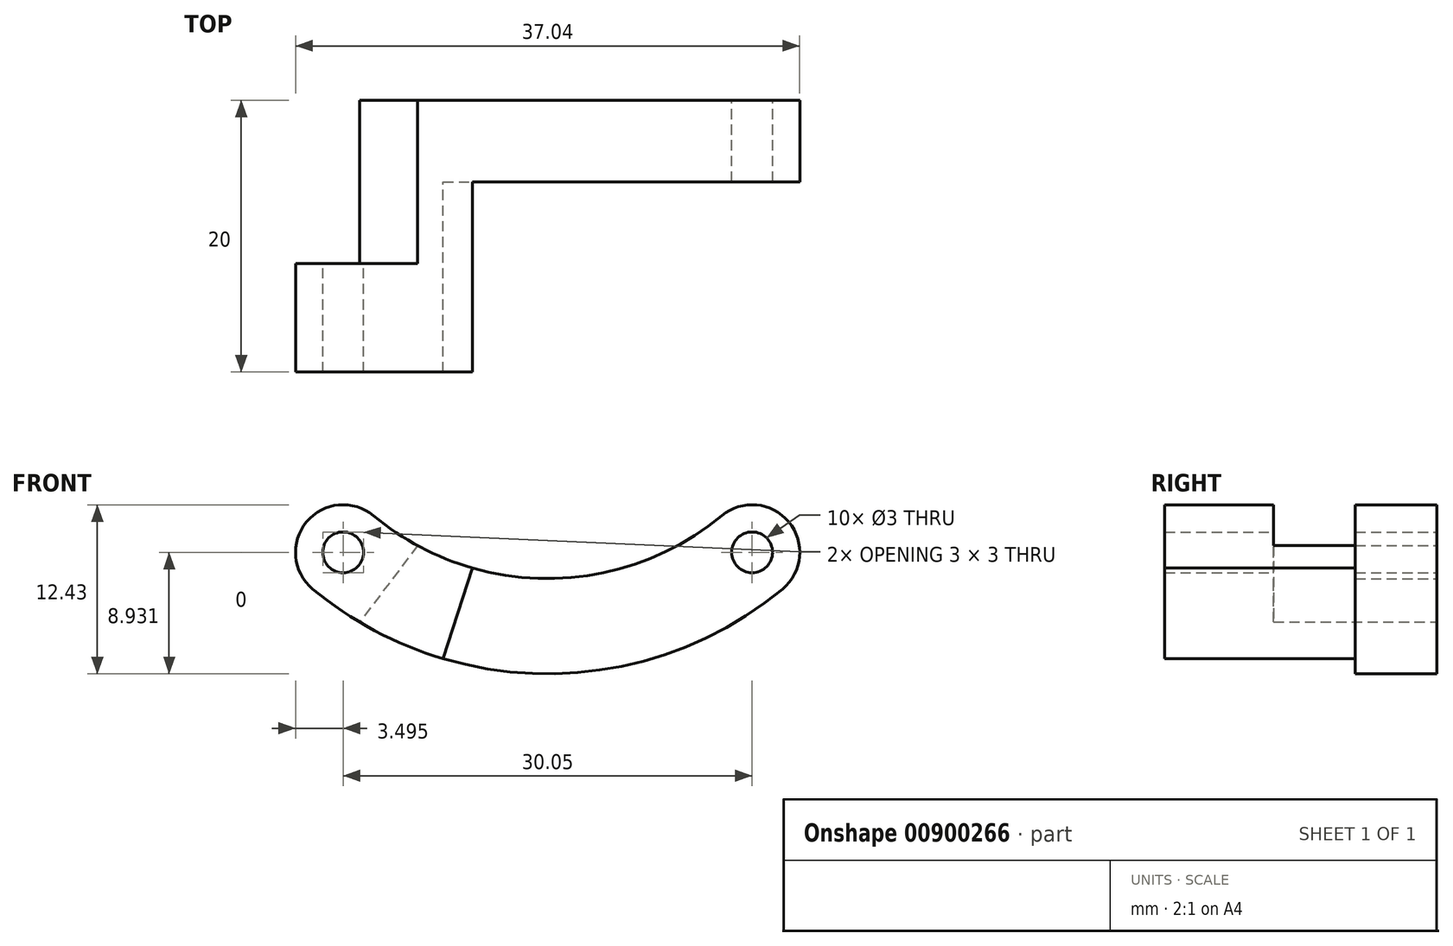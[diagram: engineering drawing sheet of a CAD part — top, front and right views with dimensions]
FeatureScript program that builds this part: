
annotation { "Feature Type Name" : "Feature", "Feature Type Description" : "" }
export const myFeature = defineFeature(function(context is Context, id is Id, definition is map)
    precondition{}
    {
        {
            var Q0;
            Q0=qCreatedBy(makeId("Front.planeOp"),FACE);
            var sketch = newSketch(context, id + "F0", { "sketchPlane" : qUnion([Q0])});
            skArc(sketch, "E0", {"start": v(-12.79, -15.38) * mm, "mid": v(0, -20) * mm, "end": v(12.79, -15.38) * mm});
            skArc(sketch, "E1", {"start": v(-17.26, -20.76) * mm, "mid": v(0, -27) * mm, "end": v(17.26, -20.76) * mm});
            skArc(sketch, "E2", {"start": v(-15.02, -18.07) * mm, "mid": v(0, -23.5) * mm, "end": v(15.03, -18.07) * mm});
            skArc(sketch, "E3", {"start": v(17.26, -20.76) * mm, "mid": v(17.72, -15.83) * mm, "end": v(12.79, -15.38) * mm});
            skArc(sketch, "E4", {"start": v(-12.79, -15.38) * mm, "mid": v(-17.72, -15.83) * mm, "end": v(-17.26, -20.76) * mm});
            skCircle(sketch, "E5", {"center": v(-15.02, -18.07) * mm, "radius": 1.5 * mm});
            skCircle(sketch, "E6", {"center": v(15.03, -18.07) * mm, "radius": 1.5 * mm});
            skSolve(sketch);
        }
        {
            var Q0;
            Q0 = qSketchRegion(id + "F0", true);
            extrude(context, id + "F1", {"entities" : qUnion([Q0]), "endBound" : BoundingType.SYMMETRIC, "depth" : 20 * mm, "offsetDistance" : 25.4 * mm});
        }
        {
            var Q0;
            Q0=makeQuery(id+"F1.opExtrude","CAP_FACE",FACE,{"disambiguationData":[OSD([sQuery(id+"F0.wireOp",EDGE,"E0"),sQuery(id+"F0.wireOp",EDGE,"E1"),sQuery(id+"F0.wireOp",EDGE,"E3"),sQuery(id+"F0.wireOp",EDGE,"E4"),sQuery(id+"F0.wireOp",EDGE,"E5"),sQuery(id+"F0.wireOp",EDGE,"E6")])],"isStart":false});
            var sketch = newSketch(context, id + "F2", { "sketchPlane" : qUnion([Q0])});
            skLineSegment(sketch, "E7", {"start": v(-9.15, -30.5) * mm, "end": v(-2.4, -9.43) * mm});
            skLineSegment(sketch, "E8", {"start": v(-2.4, -9.43) * mm, "end": v(30.04, -11.8) * mm});
            skLineSegment(sketch, "E9", {"start": v(30.04, -11.8) * mm, "end": v(24.73, -32) * mm});
            skLineSegment(sketch, "E10", {"start": v(24.73, -32) * mm, "end": v(-9.15, -30.5) * mm});
            skSolve(sketch);
        }
        {
            var Q0;
            Q0 = qSketchRegion(id + "F2", true);
            extrude(context, id + "F3", {"entities" : qUnion([Q0]), "operationType" : NewBodyOperationType.REMOVE, "oppositeDirection" : true, "depth" : 14 * mm, "offsetDistance" : 25.4 * mm});
        }
        {
            var Q0;
            Q0=makeQuery(id+"F1.opExtrude","CAP_FACE",FACE,{"disambiguationData":[OSD([sQuery(id+"F0.wireOp",EDGE,"E0"),sQuery(id+"F0.wireOp",EDGE,"E1"),sQuery(id+"F0.wireOp",EDGE,"E3"),sQuery(id+"F0.wireOp",EDGE,"E4"),sQuery(id+"F0.wireOp",EDGE,"E5"),sQuery(id+"F0.wireOp",EDGE,"E6")])],"isStart":true});
            var sketch = newSketch(context, id + "F4", { "sketchPlane" : qUnion([Q0])});
            skLineSegment(sketch, "E11", {"start": v(6.43, -13.47) * mm, "end": v(17.8, -28.46) * mm});
            skLineSegment(sketch, "E12", {"start": v(17.8, -28.46) * mm, "end": v(37.61, -8.65) * mm});
            skLineSegment(sketch, "E13", {"start": v(37.61, -8.65) * mm, "end": v(13.5, -6.4) * mm});
            skLineSegment(sketch, "E14", {"start": v(13.5, -6.4) * mm, "end": v(6.43, -13.47) * mm});
            skSolve(sketch);
        }
        {
            var Q0;
            Q0 = qSketchRegion(id + "F4", true);
            extrude(context, id + "F5", {"entities" : qUnion([Q0]), "operationType" : NewBodyOperationType.REMOVE, "oppositeDirection" : true, "depth" : 12 * mm, "offsetDistance" : 25.4 * mm});
        }
    });
